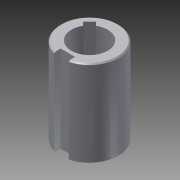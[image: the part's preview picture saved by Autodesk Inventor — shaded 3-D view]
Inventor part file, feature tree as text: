
AUTODESK INVENTOR PART (.ipt)
format: ipt  version: 2014 SP1 (Build 180222100, 222)  size: 108,032 bytes
history: native  units: in
note: dims shown in document units (in); Inventor stores cm internally (conversion verified against a paired STEP export)
features: extrude x1, chamfer x1, sketch x1
ambient origin geometry x8: Origin, YZ Plane, XZ Plane, XY Plane, X Axis, Y Axis, Z Axis, Center Point
bodies: Solid1 (feature_tree)
feature tree (3):
  extrude  "Extrusion1"  Depth=0.315in
  chamfer  "Chamfer1"  Distance=0.125in
  sketch  "Sketch1"  dims[d0=0.5in d1=0.315in d4=0.125in d5=45.0deg d6=0.0787in d8=0.0625in d9=0.0394in d10=0.75in d11=0.0in d12=0.01in d13=0.125in d14=45.0deg]
